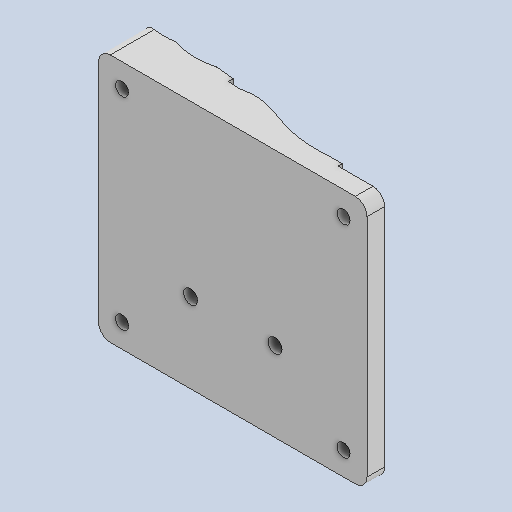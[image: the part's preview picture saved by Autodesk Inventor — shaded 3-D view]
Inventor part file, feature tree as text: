
AUTODESK INVENTOR PART (.ipt)
format: ipt  version: 2023 (Build 270158000, 158)  size: 262,656 bytes
history: native  units: mm
features: other x7, reference x6, extrude x3, sketch x2, plane x1, fillet x1
ambient origin geometry x8: Origin, YZ Plane, XZ Plane, XY Plane, X Axis, Y Axis, Z Axis, Center Point
bodies: Solid1 (feature_tree)
feature tree (20):
  plane  "Work Plane1"
  extrude  "Extrusion1"  Depth=22.0mm
  extrude  "Extrusion2"  Depth=5.0mm
  fillet  "Fillet1"  Radius=2.8mm
  extrude  "Extrusion3"  Depth=20.0mm
  reference  "Reference3"
  reference  "Reference4"
  sketch  "Sketch2"  dims[d0=10.15mm d1=22.0mm]
  reference  "Reference6"
  reference  "Reference7"
  sketch  "Sketch3"  dims[d2=5.0mm d3=5.0mm d4=2.8mm d5=20.0mm d7=47.188mm d8=20.0mm d10=43.043mm d13=21.749mm d14=0.0mm d15=0.0mm d16=0.0mm d17=2.5mm d18=0.0mm d19=67.251mm d20=0.0mm d23=0.5mm d24=0.5mm]
  reference  "Reference10"
  reference  "Reference11"
  parser-record x1  (decoder bookkeeping rows leaked as tree rows — omitted from the tree; the rows remain in map.json)
  other  "Assembly_V6.iam"
  other  "rack_V6:1"
  other  "pinion_V6:2"
  other  "moulding:1"
  other  "motor:2"
  other  "motor:1"
note: 1 file-system path scrubbed to <path> (originals preserved in map.json)
